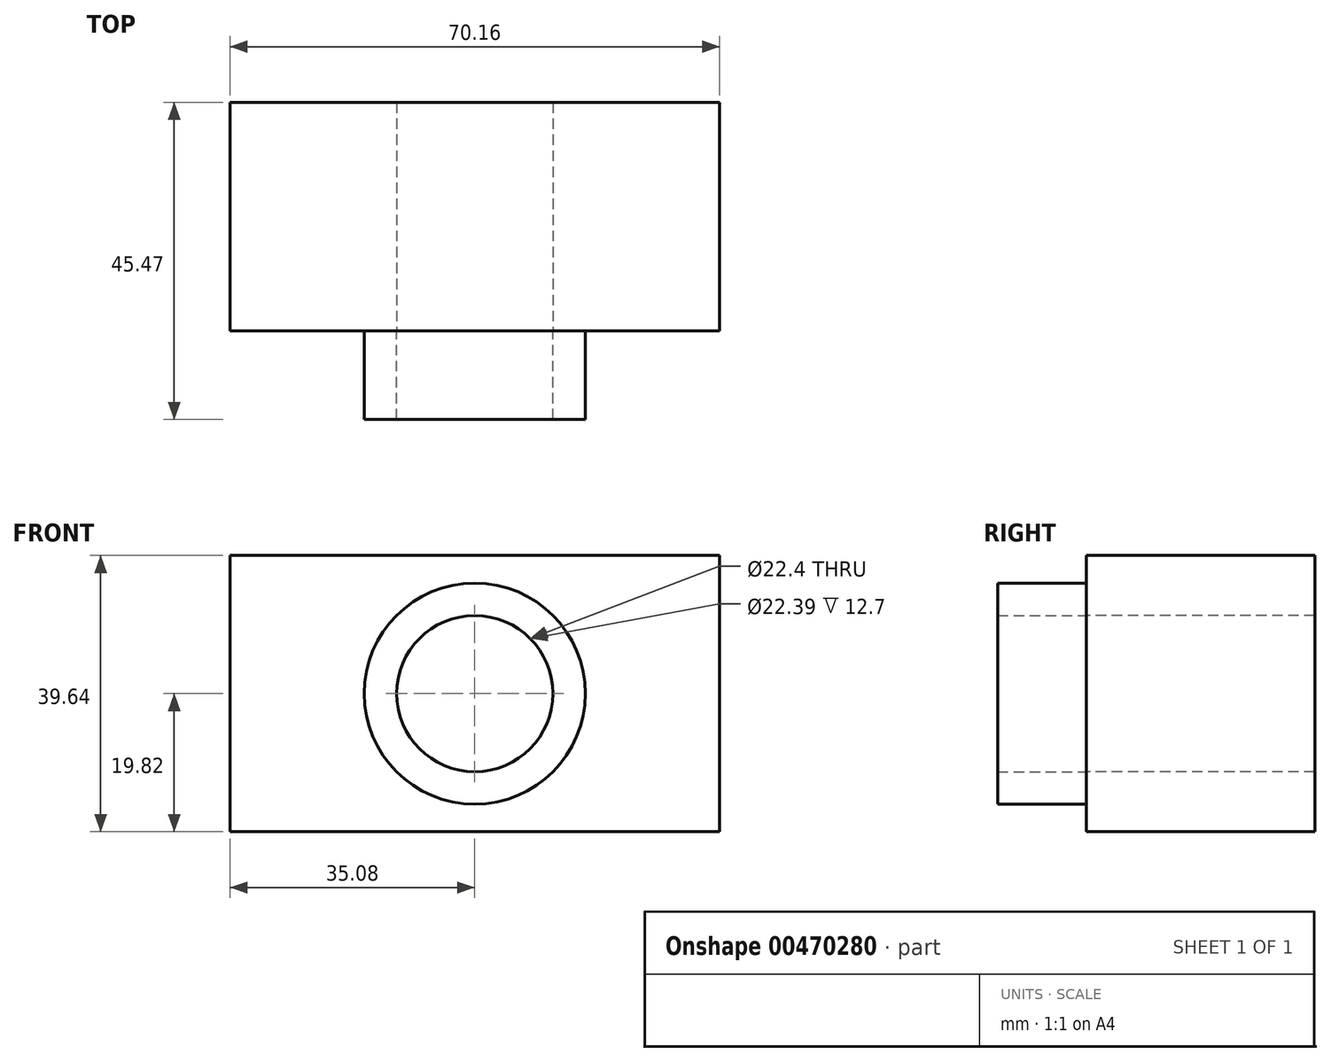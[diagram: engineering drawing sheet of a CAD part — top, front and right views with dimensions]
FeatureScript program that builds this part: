
annotation { "Feature Type Name" : "Feature", "Feature Type Description" : "" }
export const myFeature = defineFeature(function(context is Context, id is Id, definition is map)
    precondition{}
    {
        {
            var Q0;
            Q0=qCreatedBy(makeId("Front.planeOp"),FACE);
            var sketch = newSketch(context, id + "F0", { "sketchPlane" : qUnion([Q0])});
            skLineSegment(sketch, "E0.bottom", {"start": v(35.08, 19.82) * mm, "end": v(-35.08, 19.82) * mm});
            skLineSegment(sketch, "E0.top", {"start": v(35.08, -19.82) * mm, "end": v(-35.08, -19.82) * mm});
            skLineSegment(sketch, "E0.left", {"start": v(35.08, 19.82) * mm, "end": v(35.08, -19.82) * mm});
            skLineSegment(sketch, "E0.right", {"start": v(-35.08, 19.82) * mm, "end": v(-35.08, -19.82) * mm});
            skPoint(sketch, "E0.middle", {"position": v(0, 0) * mm});
            skSolve(sketch);
        }
        {
            var Q0;
            Q0=makeQuery(id+"F0.imprint","IMPRINT",FACE,{"disambiguationData":[TD([[makeQuery(id+"F0.imprint","IMPRINT",EDGE,{"derivedFrom":sQuery(id+"F0.wireOp",EDGE,"E0.bottom")}),1.0]])]});
            extrude(context, id + "F1", {"entities" : qUnion([Q0]), "oppositeDirection" : true, "depth" : 32.77 * mm});
        }
        {
            var Q0;
            Q0=makeQuery(id+"F1.opExtrude","CAP_FACE",FACE,{"disambiguationData":[OSD([sQuery(id+"F0.wireOp",EDGE,"E0.bottom"),sQuery(id+"F0.wireOp",EDGE,"E0.top"),sQuery(id+"F0.wireOp",EDGE,"E0.left"),sQuery(id+"F0.wireOp",EDGE,"E0.right")])],"isStart":true});
            var sketch = newSketch(context, id + "F2", { "sketchPlane" : qUnion([Q0])});
            skCircle(sketch, "E1", {"center": v(0, 0) * mm, "radius": 15.85 * mm});
            skCircle(sketch, "E2", {"center": v(0, 0) * mm, "radius": 11.2 * mm});
            skSolve(sketch);
        }
        {
            var Q0;
            Q0=sQuery(id+"F2.wireOp",VERTEX,"E1.center");
            var Q1;
            Q1=makeQuery(id+"F1.opExtrude","SWEPT_BODY",BODY,{"disambiguationData":[OSD([sQuery(id+"F0.wireOp",EDGE,"E0.bottom"),sQuery(id+"F0.wireOp",EDGE,"E0.top"),sQuery(id+"F0.wireOp",EDGE,"E0.left"),sQuery(id+"F0.wireOp",EDGE,"E0.right")])]});
            hole(context, id + "F3", {"style" : HoleStyle.SIMPLE, "endStyle" : HoleEndStyle.THROUGH, "holeDiameter" : 22.4 * mm, "isTappedThrough" : true, "tappedDepth" : 12.7 * mm, "tapClearance" : 3, "locations" : qUnion([Q0]), "scope" : qUnion([Q1])});
        }
        {
            var Q0;
            Q0 = qSketchRegion(id + "F2", true);
            extrude(context, id + "F4", {"entities" : qUnion([Q0]), "operationType" : NewBodyOperationType.ADD, "depth" : 12.7 * mm});
        }
    });
